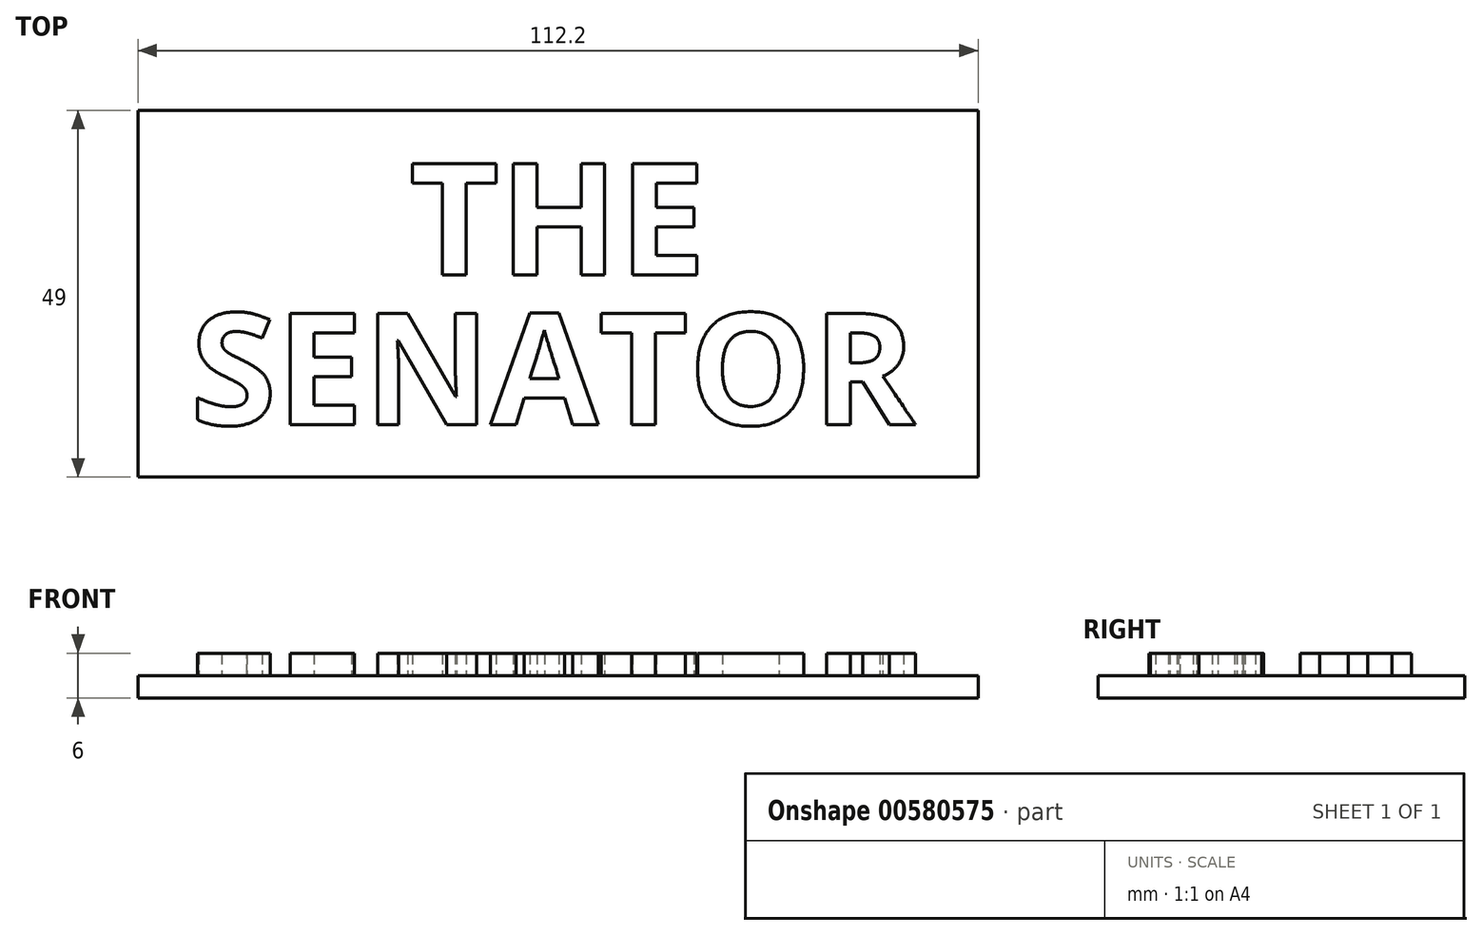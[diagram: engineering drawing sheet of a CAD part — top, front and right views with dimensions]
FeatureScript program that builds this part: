
annotation { "Feature Type Name" : "Feature", "Feature Type Description" : "" }
export const myFeature = defineFeature(function(context is Context, id is Id, definition is map)
    precondition{}
    {
        {
            var Q0;
            Q0=qCreatedBy(makeId("Top.planeOp"),FACE);
            var sketch = newSketch(context, id + "F0", { "sketchPlane" : qUnion([Q0])});
            skLineSegment(sketch, "E0.bottom", {"start": v(-56.1, 24.5) * mm, "end": v(56.1, 24.5) * mm});
            skLineSegment(sketch, "E0.top", {"start": v(-56.1, -24.5) * mm, "end": v(56.1, -24.5) * mm});
            skLineSegment(sketch, "E0.left", {"start": v(-56.1, 24.5) * mm, "end": v(-56.1, -24.5) * mm});
            skLineSegment(sketch, "E0.right", {"start": v(56.1, 24.5) * mm, "end": v(56.1, -24.5) * mm});
            skSolve(sketch);
        }
        {
            var Q0;
            Q0 = qSketchRegion(id + "F0", true);
            extrude(context, id + "F1", {"entities" : qUnion([Q0]), "depth" : 3 * mm, "offsetDistance" : 25 * mm});
        }
        {
            var Q0;
            Q0=makeQuery(id+"F1.opExtrude","CAP_FACE",FACE,{"disambiguationData":[OSD([sQuery(id+"F0.wireOp",EDGE,"E0.bottom"),sQuery(id+"F0.wireOp",EDGE,"E0.top"),sQuery(id+"F0.wireOp",EDGE,"E0.left"),sQuery(id+"F0.wireOp",EDGE,"E0.right")])],"isStart":false});
            var sketch = newSketch(context, id + "F2", { "sketchPlane" : qUnion([Q0])});
            skText(sketch, "E1", { "text": "THE", "fontName": "OpenSans-Bold.ttf"});
            skText(sketch, "E2", { "text": "SENATOR", "fontName": "OpenSans-Bold.ttf"});
            const initialGuessF2  = {"E1": [-0.0199, 0.0025, 1, 0, 0.015], "E2": [-0.0491, -0.0175, 1, 0, 0.015]};
            skSetInitialGuess(sketch, initialGuessF2);
            skSolve(sketch);
        }
        {
            var Q0;
            Q0 = qSketchRegion(id + "F2", true);
            extrude(context, id + "F3", {"entities" : qUnion([Q0]), "operationType" : NewBodyOperationType.ADD, "depth" : 3 * mm, "offsetDistance" : 25 * mm});
        }
    });
